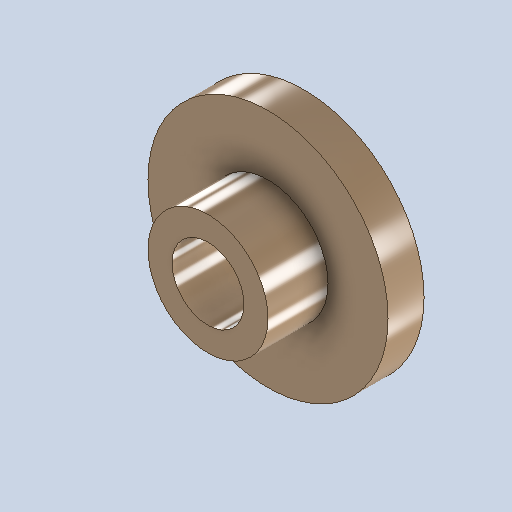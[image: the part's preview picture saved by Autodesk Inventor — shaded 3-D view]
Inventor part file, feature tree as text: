
AUTODESK INVENTOR PART (.ipt)
format: ipt  version: 2025.1 (Build 291241000, 241)  size: 134,656 bytes
history: native  units: mm
features: other x3, sketch x2
ambient origin geometry x8: Origin, YZ Plane, XZ Plane, XY Plane, X Axis, Y Axis, Z Axis, Center Point
bodies: Solid1 (feature_tree)
feature tree (5):
  other  "130 part 3.ipt"
  other  "Solid1::130 part 3.ipt"
  other  "TaggingFeature1"
  sketch  "Sketch1"  dims[d0=10.0mm]
  sketch  "Sketch2"
